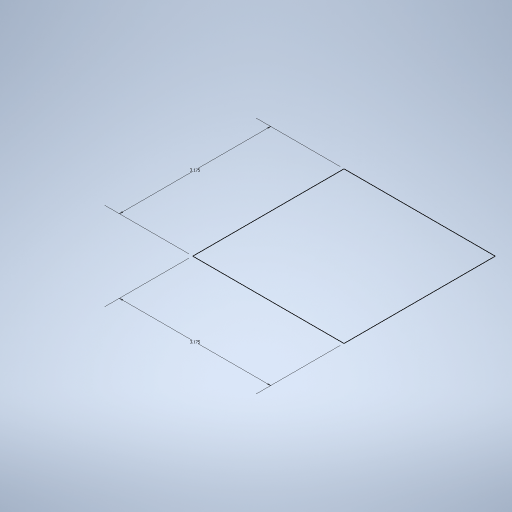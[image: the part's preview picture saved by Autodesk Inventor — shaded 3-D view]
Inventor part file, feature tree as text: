
AUTODESK INVENTOR PART (.ipt)
format: ipt  version: 2023 (Build 270158000, 158)  size: 234,496 bytes
history: native  units: mm
features: sketch x1
ambient origin geometry x8: Origin, YZ Plane, XZ Plane, XY Plane, X Axis, Y Axis, Z Axis, Center Point
feature tree (1):
  sketch  "Sketch1"  dims[d0=3.175mm d1=3.175mm]
